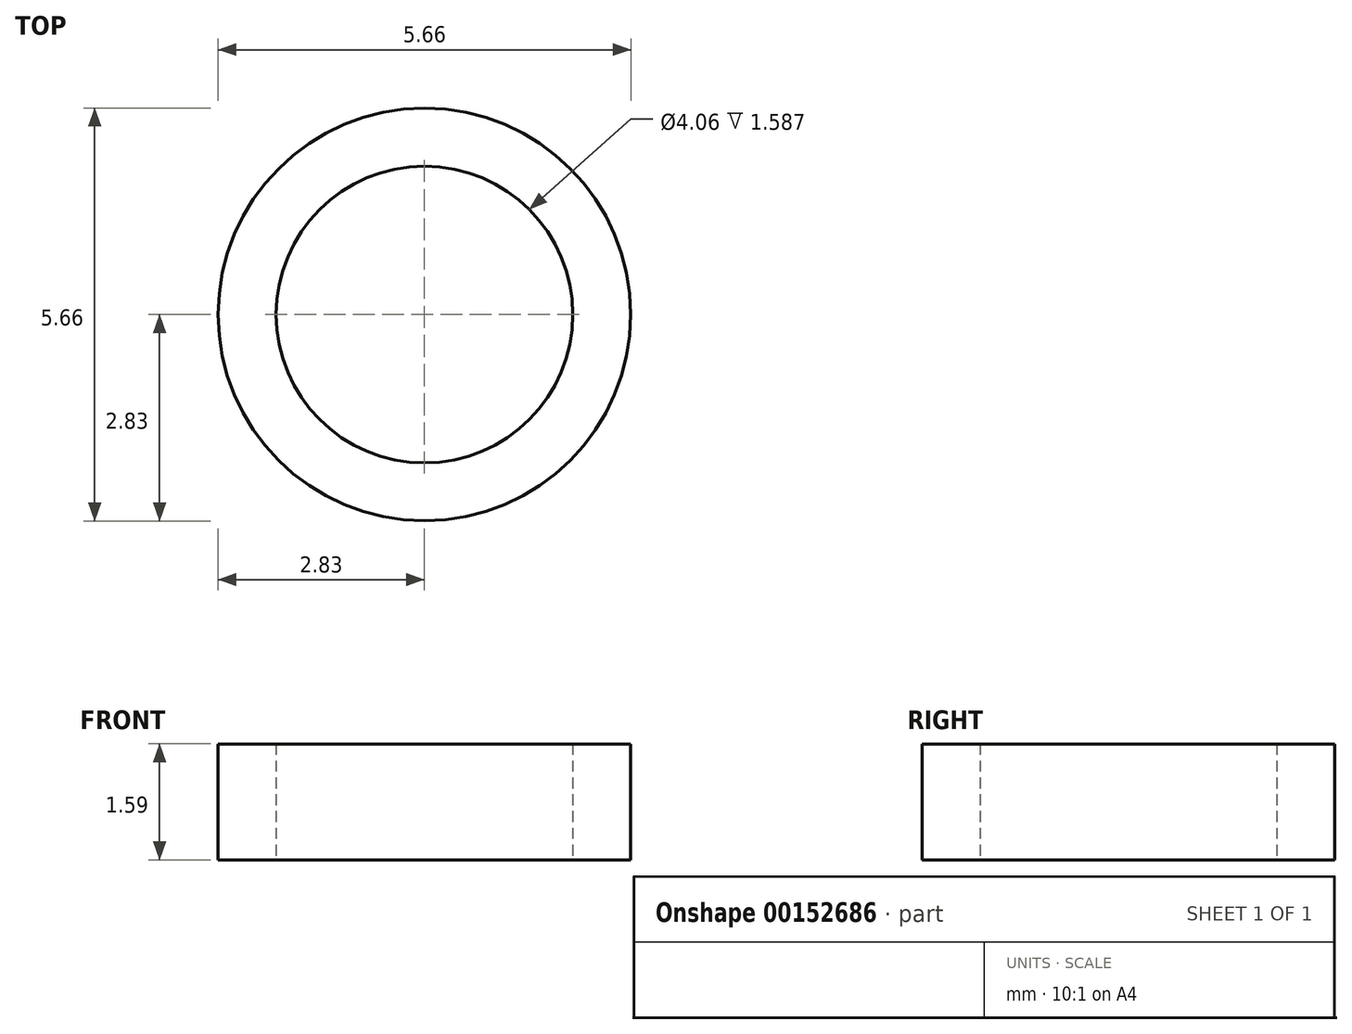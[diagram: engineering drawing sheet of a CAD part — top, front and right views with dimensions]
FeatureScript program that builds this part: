
annotation { "Feature Type Name" : "Feature", "Feature Type Description" : "" }
export const myFeature = defineFeature(function(context is Context, id is Id, definition is map)
    precondition{}
    {
        {
            var Q0;
            Q0=qCreatedBy(makeId("Top.planeOp"),FACE);
            var sketch = newSketch(context, id + "F0", { "sketchPlane" : qUnion([Q0])});
            skCircle(sketch, "E0", {"center": v(0, 0) * mm, "radius": 2.03 * mm});
            skCircle(sketch, "E1", {"center": v(0, 0) * mm, "radius": 2.83 * mm});
            skSolve(sketch);
        }
        {
            var Q0;
            Q0 = qSketchRegion(id + "F0", true);
            extrude(context, id + "F1", {"entities" : qUnion([Q0]), "depth" : 1.59 * mm});
        }
    });
